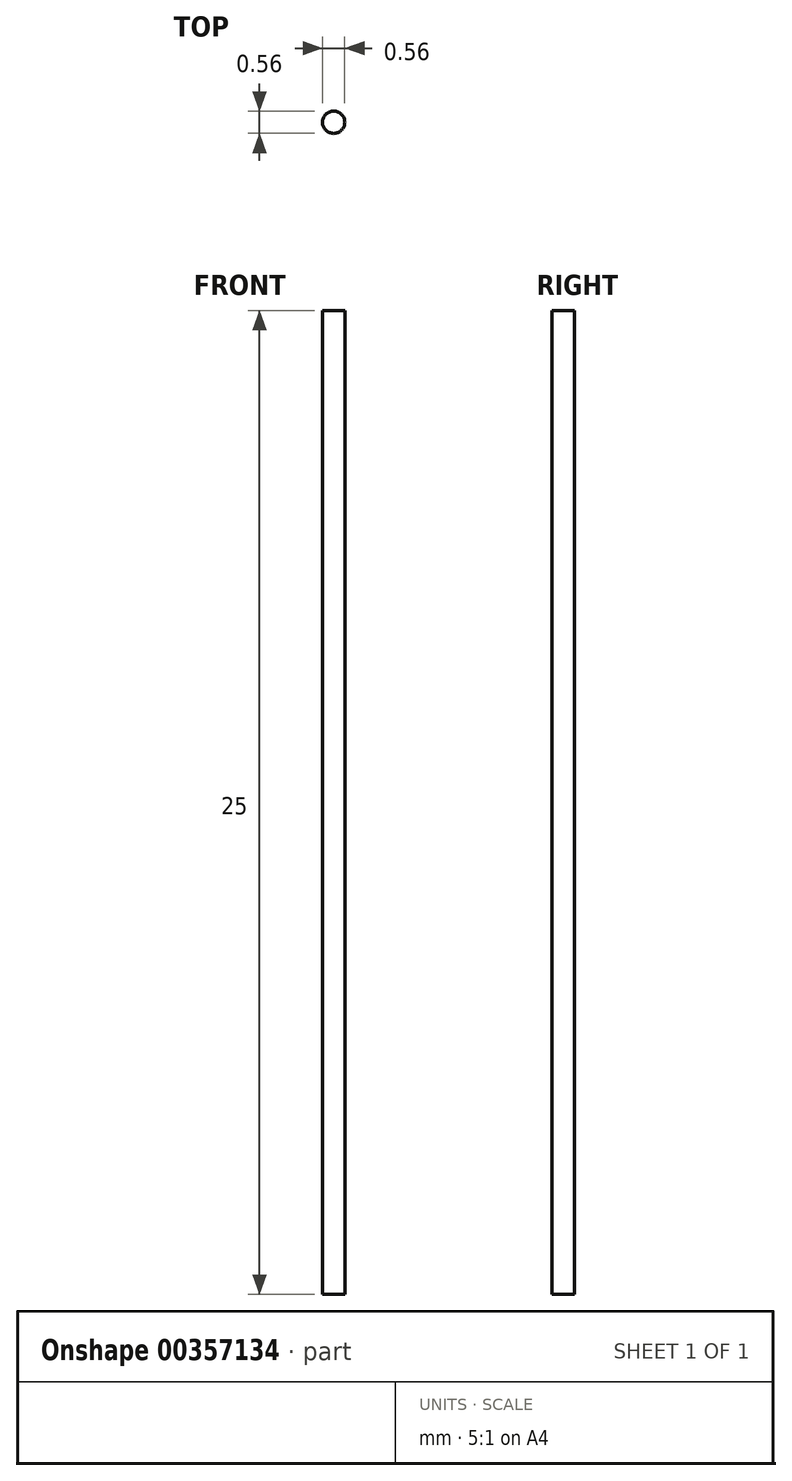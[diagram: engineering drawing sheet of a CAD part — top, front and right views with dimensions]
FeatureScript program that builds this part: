
annotation { "Feature Type Name" : "Feature", "Feature Type Description" : "" }
export const myFeature = defineFeature(function(context is Context, id is Id, definition is map)
    precondition{}
    {
        {
            var Q0;
            Q0=qCreatedBy(makeId("Top.planeOp"),FACE);
            var sketch = newSketch(context, id + "F0", { "sketchPlane" : qUnion([Q0])});
            skCircle(sketch, "E0", {"center": v(0, 0) * mm, "radius": 0.28 * mm});
            skSolve(sketch);
        }
        {
            var Q0;
            Q0 = qSketchRegion(id + "F0", true);
            extrude(context, id + "F1", {"entities" : qUnion([Q0]), "endBound" : BoundingType.SYMMETRIC, "depth" : 25 * mm});
        }
    });
